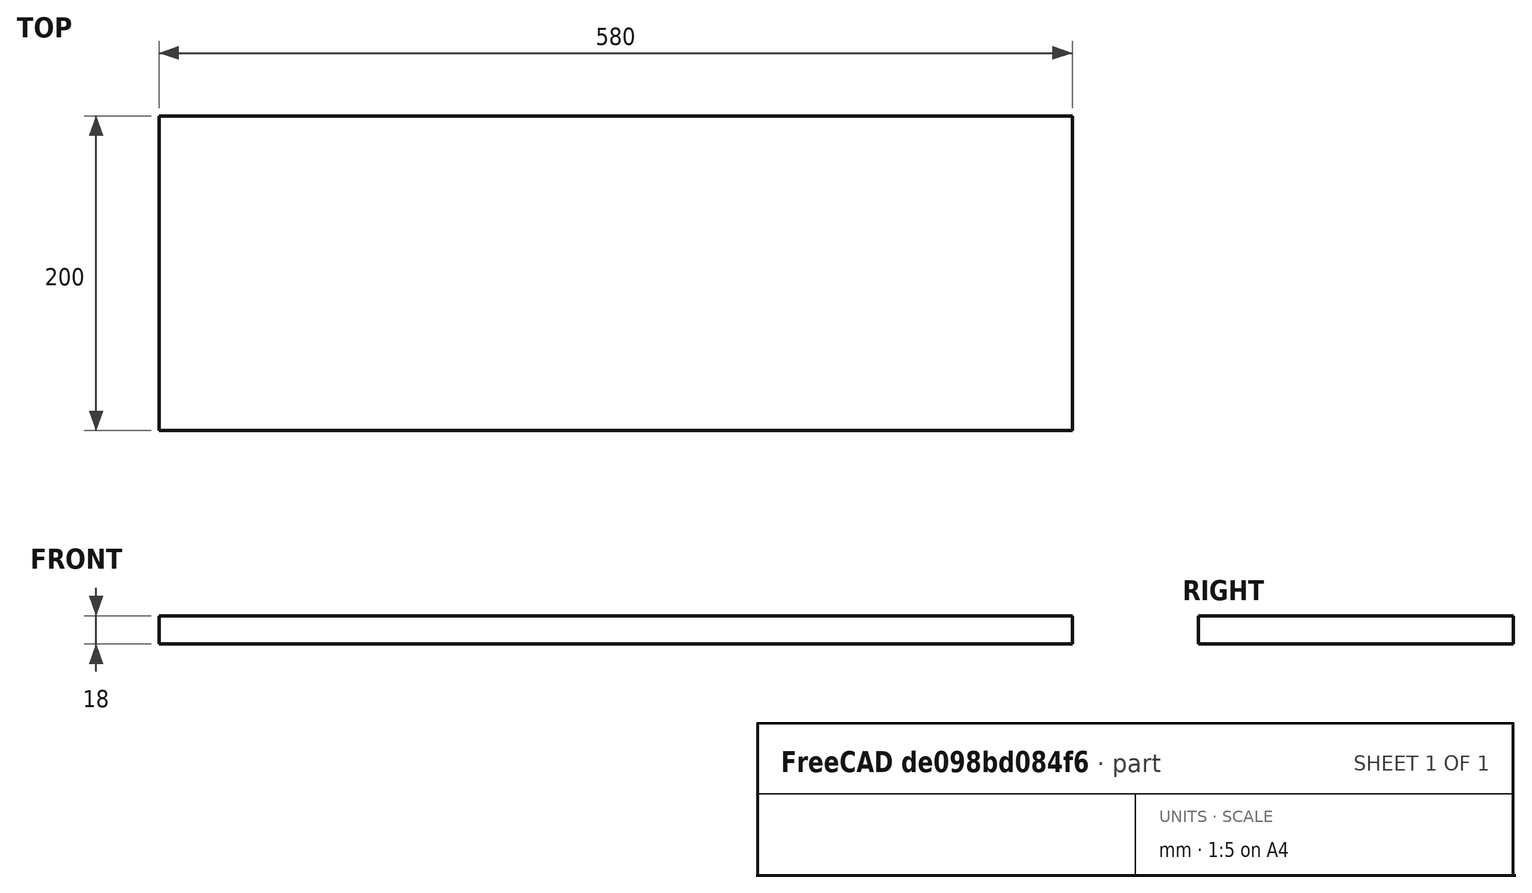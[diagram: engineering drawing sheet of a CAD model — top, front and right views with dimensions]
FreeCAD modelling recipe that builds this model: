
FCSTD DOCUMENT  (FreeCAD 0.18R4 (GitTag))
Label: shelf
License: All rights reserved
LicenseURL: http://en.wikipedia.org/wiki/All_rights_reserved
objects: Sketcher::SketchObject×1, PartDesign::Pad×1, PartDesign::Body×1, App::Part×1
note: 4 computed .brp shape members not serialized (recipe doc carries the construction recipe); baked Part::Feature solids carry a one-line shape summary decoded from their .brp

FEATURE [Sketcher::SketchObject] Sketch
  MapMode = 5
  Placement = pos=(0,0,0) rot=(0.57735,0.57735,0.57735;2.0944rad)
  Support = -> [YZ_Plane001]
  sketch-geometry (4):
    g0: LineSegment StartX=0 StartY=18 StartZ=0 EndX=-200 EndY=18 EndZ=0
    g1: LineSegment StartX=-200 StartY=18 StartZ=0 EndX=-200 EndY=0 EndZ=0
    g2: LineSegment StartX=-200 StartY=0 StartZ=0 EndX=0 EndY=0 EndZ=0
    g3: LineSegment StartX=0 StartY=0 StartZ=0 EndX=0 EndY=18 EndZ=0
  constraints (11):
    c: Coincident(g0,g1)
    c: Coincident(g1,g2)
    c: Coincident(g2,g3)
    c: Coincident(g3,g0)
    c: Horizontal(g0)
    c: Horizontal(g2)
    c: Vertical(g1)
    c: Vertical(g3)
    c: DistanceY(g0) = 18
    c: DistanceX(g0,g0) = 200
    c: Coincident(g2,g-1)
FEATURE [PartDesign::Pad] Pad
  Length = 580
  Length2 = 100
  Placement = pos=(0,0,0) rot=(0.57735,0.57735,0.57735;2.0944rad)
  Profile = -> Sketch
  Type = 0
FEATURE [PartDesign::Body] Body
  Group = -> [Sketch,Pad]
  Origin = -> Origin001
  Tip = -> Pad
FEATURE [App::Part] Part
  Group = -> [Body]
  Origin = -> Origin
